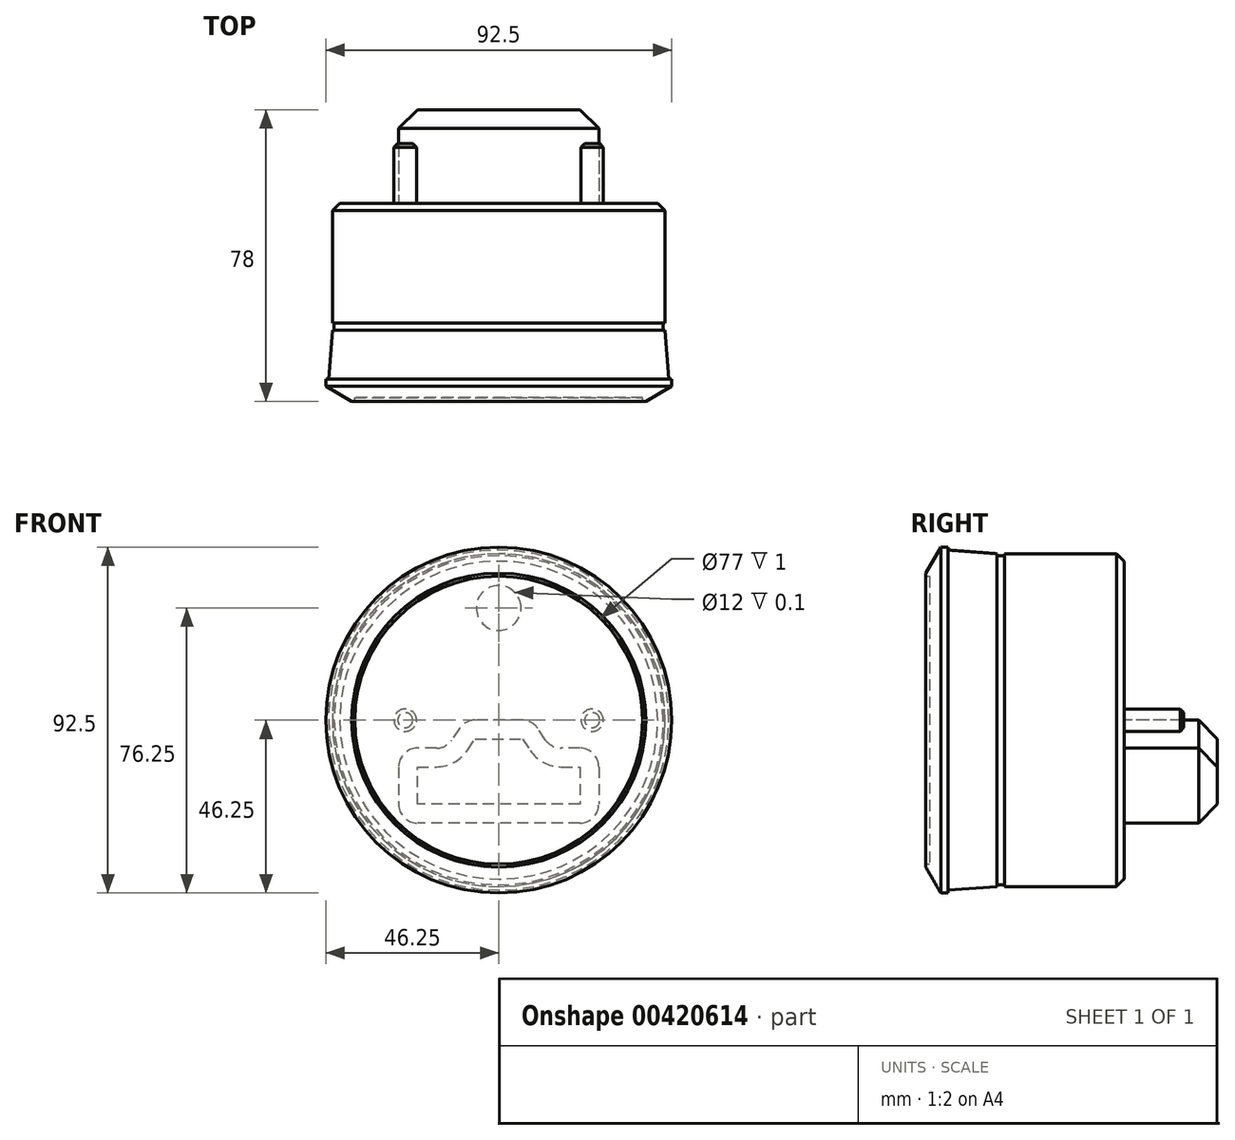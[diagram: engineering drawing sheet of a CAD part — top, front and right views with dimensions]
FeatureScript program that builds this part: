
annotation { "Feature Type Name" : "Feature", "Feature Type Description" : "" }
export const myFeature = defineFeature(function(context is Context, id is Id, definition is map)
    precondition{}
    {
        {
            var Q0;
            Q0=qCreatedBy(makeId("Top.planeOp"),FACE);
            var sketch = newSketch(context, id + "F0", { "sketchPlane" : qUnion([Q0])});
            skLineSegment(sketch, "E0", {"start": v(0, 21.71) * mm, "end": v(0, 0) * mm, "construction": true});
            skLineSegment(sketch, "E1", {"start": v(-46.25, -53) * mm, "end": v(-46.25, -47) * mm});
            skLineSegment(sketch, "E2", {"start": v(-46.25, -47) * mm, "end": v(-45.5, -47) * mm});
            skLineSegment(sketch, "E3", {"start": v(-45.5, -47) * mm, "end": v(-45.5, 0) * mm, "construction": true});
            skLineSegment(sketch, "E4", {"start": v(0, -52) * mm, "end": v(0, 0) * mm});
            skLineSegment(sketch, "E5", {"start": v(-46.25, -53) * mm, "end": v(-38.5, -53) * mm});
            skLineSegment(sketch, "E6", {"start": v(-38.5, -53) * mm, "end": v(-38.5, -52) * mm});
            skLineSegment(sketch, "E7", {"start": v(-38.5, -52) * mm, "end": v(0, -52) * mm});
            skLineSegment(sketch, "E8", {"start": v(-45.5, -47) * mm, "end": v(-44.5, -34) * mm});
            skLineSegment(sketch, "E9", {"start": v(-44.5, -34) * mm, "end": v(-44, -34) * mm});
            skLineSegment(sketch, "E10", {"start": v(-44, -34) * mm, "end": v(-44, -32) * mm});
            skLineSegment(sketch, "E11", {"start": v(-44, -32) * mm, "end": v(-44.5, -32) * mm});
            skLineSegment(sketch, "E12", {"start": v(-44.5, -32) * mm, "end": v(-44.5, 0) * mm});
            skLineSegment(sketch, "E13", {"start": v(-44.5, 0) * mm, "end": v(0, 0) * mm});
            skSolve(sketch);
        }
        {
            var Q0;
            Q0=qSketchRegion(id+"F0",true);
            var Q1;
            Q1=sQuery(id+"F0.wireOp",EDGE,"E0");
            revolve(context, id + "F1", {"entities" : qUnion([Q0]), "axis" : qUnion([Q1]), "revolveType" : RevolveType.FULL});
        }
        {
            var Q0;
            Q0=makeQuery(id+"F1.opRevolve","SWEPT_FACE",FACE,{"disambiguationData":[OSD([sQuery(id+"F0.wireOp",EDGE,"E13")])]});
            var sketch = newSketch(context, id + "F2", { "sketchPlane" : qUnion([Q0])});
            skCircle(sketch, "E14", {"center": v(-25, 0) * mm, "radius": 3 * mm});
            skCircle(sketch, "E15", {"center": v(25, 0) * mm, "radius": 3 * mm});
            skLineSegment(sketch, "E16", {"start": v(-25, 0) * mm, "end": v(25, 0) * mm, "construction": true});
            skSolve(sketch);
        }
        {
            var Q0;
            Q0=qSketchRegion(id+"F2",true);
            extrude(context, id + "F3", {"entities" : qUnion([Q0]), "operationType" : NewBodyOperationType.ADD, "depth" : 16 * mm, "offsetDistance" : 25 * mm});
        }
        {
            var Q0;
            Q0=makeQuery(id+"F1.opRevolve","SWEPT_FACE",FACE,{"disambiguationData":[OSD([sQuery(id+"F0.wireOp",EDGE,"E13")])]});
            var sketch = newSketch(context, id + "F4", { "sketchPlane" : qUnion([Q0])});
            skLineSegment(sketch, "E17.bottom", {"start": v(-26.75, -7.5) * mm, "end": v(26.75, -7.5) * mm, "construction": true});
            skLineSegment(sketch, "E17.top", {"start": v(-26.75, -27.5) * mm, "end": v(26.75, -27.5) * mm});
            skLineSegment(sketch, "E17.left", {"start": v(-26.75, -7.5) * mm, "end": v(-26.75, -27.5) * mm});
            skLineSegment(sketch, "E17.right", {"start": v(26.75, -7.5) * mm, "end": v(26.75, -27.5) * mm});
            skPoint(sketch, "E17.middle", {"position": v(0, -17.5) * mm});
            skLineSegment(sketch, "E18", {"start": v(-26.75, -7.5) * mm, "end": v(-14, -7.5) * mm});
            skLineSegment(sketch, "E19", {"start": v(-14, -7.5) * mm, "end": v(-9, 0) * mm});
            skLineSegment(sketch, "E20", {"start": v(-9, 0) * mm, "end": v(9, 0) * mm});
            skLineSegment(sketch, "E21", {"start": v(9, 0) * mm, "end": v(14, -7.5) * mm});
            skLineSegment(sketch, "E22", {"start": v(14, -7.5) * mm, "end": v(26.75, -7.5) * mm});
            skSolve(sketch);
        }
        {
            var Q0;
            Q0 = qSketchRegion(id + "F4", true);
            extrude(context, id + "F5", {"entities" : qUnion([Q0]), "operationType" : NewBodyOperationType.ADD, "depth" : 25 * mm, "offsetDistance" : 25 * mm});
        }
        {
            var Q0;
            Q0=makeQuery(id+"F3.opExtrude","CAP_EDGE",EDGE,{"disambiguationData":[OSD([sQuery(id+"F2.wireOp",EDGE,"E14")])],"isStart":false});
            var Q1;
            Q1=makeQuery(id+"F3.opExtrude","CAP_FACE",FACE,{"disambiguationData":[OSD([sQuery(id+"F2.wireOp",EDGE,"E15")])],"isStart":false});
            chamfer(context, id + "F6", {"entities" : qUnion([Q0, Q1]), "width" : 1 * mm, "tangentPropagation" : true});
        }
        {
            var Q0;
            Q0=makeQuery(id+"F1.opRevolve","SWEPT_EDGE",EDGE,{"disambiguationData":[OSD([sQuery(id+"F0.wireOp",EDGE,"E12"),sQuery(id+"F0.wireOp",EDGE,"E13")])]});
            chamfer(context, id + "F7", {"entities" : qUnion([Q0]), "width" : 2 * mm, "tangentPropagation" : true});
        }
        {
            var Q0;
            Q0=makeQuery(id+"F1.opRevolve","SWEPT_FACE",FACE,{"disambiguationData":[OSD([sQuery(id+"F0.wireOp",EDGE,"E13")])]});
            var sketch = newSketch(context, id + "F8", { "sketchPlane" : qUnion([Q0])});
            skCircle(sketch, "E23", {"center": v(0, 30) * mm, "radius": 6 * mm});
            skSolve(sketch);
        }
        {
            var Q0;
            Q0 = qSketchRegion(id + "F8", true);
            extrude(context, id + "F9", {"entities" : qUnion([Q0]), "operationType" : NewBodyOperationType.REMOVE, "oppositeDirection" : true, "depth" : 0.1 * mm, "offsetDistance" : 25 * mm});
        }
        {
            var Q0;
            Q0=makeQuery(id+"F1.opRevolve","SWEPT_EDGE",EDGE,{"disambiguationData":[OSD([sQuery(id+"F0.wireOp",EDGE,"E1"),sQuery(id+"F0.wireOp",EDGE,"E5")])]});
            chamfer(context, id + "F10", {"entities" : qUnion([Q0]), "chamferType" : ChamferType.OFFSET_ANGLE, "width" : 4 * mm, "oppositeDirection" : false, "angle" : 60 * degree});
        }
        {
            var Q0;
            Q0=makeQuery(id+"F5.opExtrude","SWEPT_EDGE",EDGE,{"disambiguationData":[OSD([sQuery(id+"F4.wireOp",EDGE,"E17.top"),sQuery(id+"F4.wireOp",EDGE,"E17.left")])]});
            var Q1;
            Q1=makeQuery(id+"F5.opExtrude","SWEPT_EDGE",EDGE,{"disambiguationData":[OSD([sQuery(id+"F4.wireOp",EDGE,"E17.left"),sQuery(id+"F4.wireOp",EDGE,"E18")])]});
            var Q2;
            Q2=makeQuery(id+"F5.opExtrude","SWEPT_EDGE",EDGE,{"disambiguationData":[OSD([sQuery(id+"F4.wireOp",EDGE,"E17.top"),sQuery(id+"F4.wireOp",EDGE,"E17.right")])]});
            var Q3;
            Q3=makeQuery(id+"F5.opExtrude","SWEPT_EDGE",EDGE,{"disambiguationData":[OSD([sQuery(id+"F4.wireOp",EDGE,"E17.right"),sQuery(id+"F4.wireOp",EDGE,"E22")])]});
            var Q4;
            Q4=makeQuery(id+"F5.opExtrude","SWEPT_EDGE",EDGE,{"disambiguationData":[OSD([sQuery(id+"F4.wireOp",EDGE,"E20"),sQuery(id+"F4.wireOp",EDGE,"E21")])]});
            var Q5;
            Q5=makeQuery(id+"F5.opExtrude","SWEPT_EDGE",EDGE,{"disambiguationData":[OSD([sQuery(id+"F4.wireOp",EDGE,"E19"),sQuery(id+"F4.wireOp",EDGE,"E20")])]});
            var Q6;
            Q6=makeQuery(id+"F5.opExtrude","SWEPT_EDGE",EDGE,{"disambiguationData":[OSD([sQuery(id+"F4.wireOp",EDGE,"E21"),sQuery(id+"F4.wireOp",EDGE,"E22")])]});
            var Q7;
            Q7=makeQuery(id+"F5.opExtrude","SWEPT_EDGE",EDGE,{"disambiguationData":[OSD([sQuery(id+"F4.wireOp",EDGE,"E18"),sQuery(id+"F4.wireOp",EDGE,"E19")])]});
            fillet(context, id + "F11", {"entities" : qUnion([Q0, Q1, Q2, Q3, Q4, Q5, Q6, Q7]), "tangentPropagation" : true, "radius" : 5 * mm, "defaultsChanged" : false, "vertexSettings" : [], "allowEdgeOverflow" : false});
        }
        {
            var Q0;
            Q0=makeQuery(id+"F5.opExtrude","CAP_FACE",FACE,{"disambiguationData":[OSD([sQuery(id+"F4.wireOp",EDGE,"E17.top"),sQuery(id+"F4.wireOp",EDGE,"E17.left"),sQuery(id+"F4.wireOp",EDGE,"E17.right"),sQuery(id+"F4.wireOp",EDGE,"E18"),sQuery(id+"F4.wireOp",EDGE,"E19"),sQuery(id+"F4.wireOp",EDGE,"E20"),sQuery(id+"F4.wireOp",EDGE,"E21"),sQuery(id+"F4.wireOp",EDGE,"E22")])],"isStart":false});
            chamfer(context, id + "F12", {"entities" : qUnion([Q0]), "width" : 5 * mm, "tangentPropagation" : true});
        }
    });
